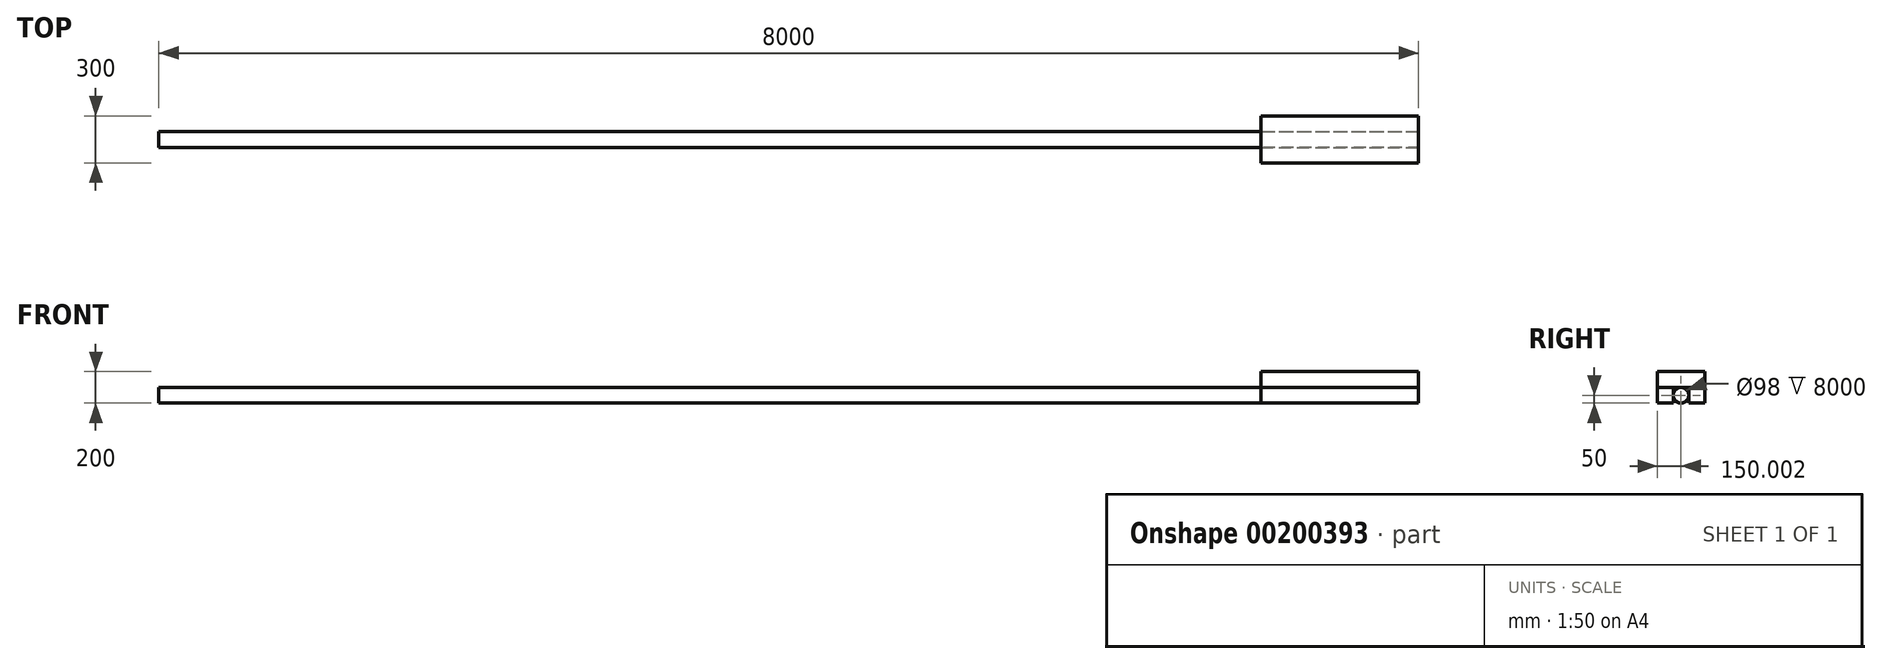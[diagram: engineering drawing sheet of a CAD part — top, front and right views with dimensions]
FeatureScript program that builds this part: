
annotation { "Feature Type Name" : "Feature", "Feature Type Description" : "" }
export const myFeature = defineFeature(function(context is Context, id is Id, definition is map)
    precondition{}
    {
        {
            var Q0;
            Q0=qCreatedBy(makeId("Top.planeOp"),FACE);
            var sketch = newSketch(context, id + "F0", { "sketchPlane" : qUnion([Q0])});
            skLineSegment(sketch, "E0.bottom", {"start": v(-84.2, 48.8) * mm, "end": v(915.8, 48.8) * mm});
            skLineSegment(sketch, "E0.top", {"start": v(-84.2, -51.2) * mm, "end": v(915.8, -51.2) * mm});
            skLineSegment(sketch, "E0.left", {"start": v(-84.2, 48.8) * mm, "end": v(-84.2, -51.2) * mm});
            skLineSegment(sketch, "E0.right", {"start": v(915.8, 48.8) * mm, "end": v(915.8, -51.2) * mm});
            skSolve(sketch);
        }
        {
            var Q0;
            Q0=makeQuery(id+"F0.imprint","IMPRINT",FACE,{"disambiguationData":[TD([[makeQuery(id+"F0.imprint","IMPRINT",EDGE,{"derivedFrom":sQuery(id+"F0.wireOp",EDGE,"E0.bottom")}),-1.0]])]});
            extrude(context, id + "F1", {"entities" : qUnion([Q0]), "depth" : 100 * mm, "offsetDistance" : 25 * mm});
        }
        {
            var Q0;
            Q0=makeQuery(id+"F1.opExtrude","SWEPT_FACE",FACE,{"disambiguationData":[OSD([sQuery(id+"F0.wireOp",EDGE,"E0.right")])]});
            var sketch = newSketch(context, id + "F2", { "sketchPlane" : qUnion([Q0])});
            skCircle(sketch, "E1", {"center": v(98.8, 50) * mm, "radius": 50 * mm});
            skPoint(sketch, "E1.centerSnap0", {"position": v(48.8, 50) * mm});
            skCircle(sketch, "E2.0", {"center": v(98.8, 50) * mm, "radius": 49 * mm});
            skSolve(sketch);
        }
        {
            var Q0;
            Q0=makeQuery(id+"F2.imprint","IMPRINT",FACE,{"disambiguationData":[TD([[makeQuery(id+"F2.imprint","IMPRINT",EDGE,{"derivedFrom":sQuery(id+"F2.wireOp",EDGE,"E1")}),1.0]])]});
            extrude(context, id + "F3", {"entities" : qUnion([Q0]), "oppositeDirection" : true, "depth" : 8000 * mm, "offsetDistance" : 25 * mm});
        }
        {
            var Q0;
            Q0=makeQuery(id+"F1.opExtrude","SWEPT_BODY",BODY,{"disambiguationData":[OSD([sQuery(id+"F0.wireOp",EDGE,"E0.bottom"),sQuery(id+"F0.wireOp",EDGE,"E0.top"),sQuery(id+"F0.wireOp",EDGE,"E0.left"),sQuery(id+"F0.wireOp",EDGE,"E0.right")])]});
            transform(context, id + "F4", {"entities" : qUnion([Q0]), "transformType" : TransformType.TRANSLATION_3D, "dx" : 0 * mm, "dy" : 200 * mm, "dz" : 0 * mm, "makeCopy" : true});
        }
        {
            var Q0;
            Q0=makeQuery(id+"F1.opExtrude","SWEPT_FACE",FACE,{"disambiguationData":[OSD([sQuery(id+"F0.wireOp",EDGE,"E0.right")])]});
            var sketch = newSketch(context, id + "F5", { "sketchPlane" : qUnion([Q0])});
            skLineSegment(sketch, "E3.bottom", {"start": v(-51.2, 100) * mm, "end": v(248.8, 100) * mm});
            skLineSegment(sketch, "E3.top", {"start": v(-51.2, 200) * mm, "end": v(248.8, 200) * mm});
            skLineSegment(sketch, "E3.left", {"start": v(-51.2, 100) * mm, "end": v(-51.2, 200) * mm});
            skLineSegment(sketch, "E3.right", {"start": v(248.8, 100) * mm, "end": v(248.8, 200) * mm});
            skSolve(sketch);
        }
        {
            var Q0;
            Q0=makeQuery(id+"F5.imprint","IMPRINT",FACE,{"disambiguationData":[TD([[makeQuery(id+"F5.imprint","IMPRINT",EDGE,{"derivedFrom":sQuery(id+"F5.wireOp",EDGE,"E3.top")}),-1.0]])]});
            extrude(context, id + "F6", {"entities" : qUnion([Q0]), "oppositeDirection" : true, "depth" : 1000 * mm, "offsetDistance" : 25 * mm});
        }
    });
